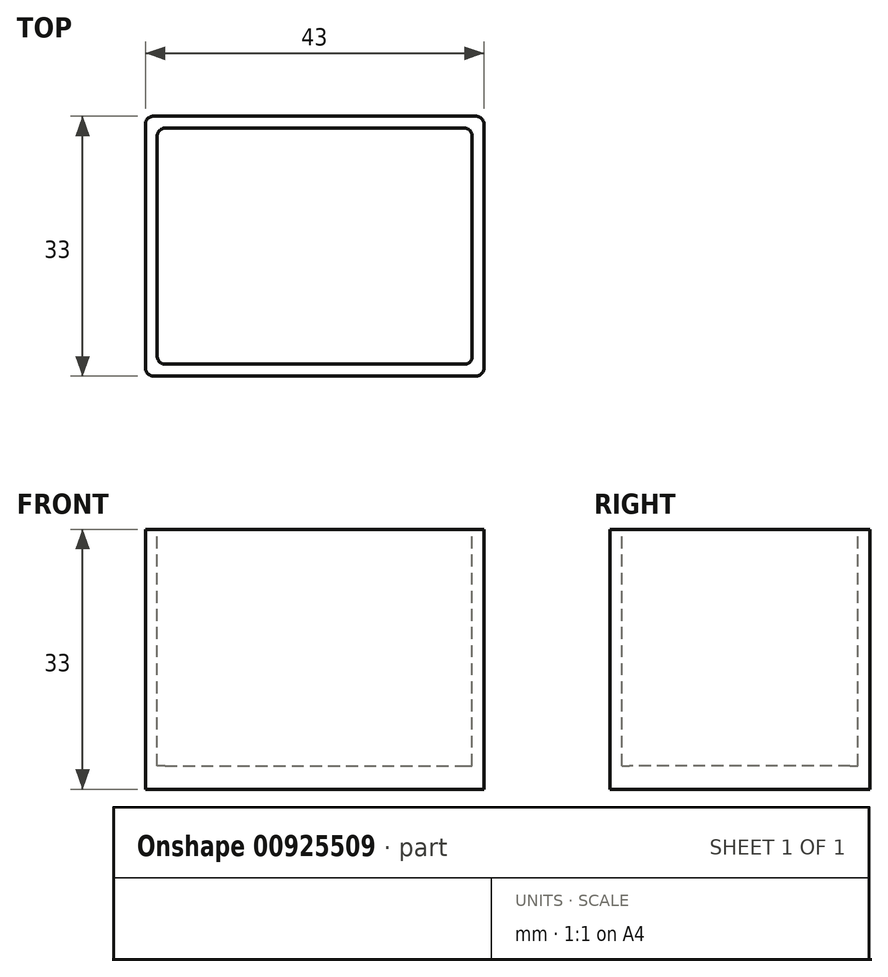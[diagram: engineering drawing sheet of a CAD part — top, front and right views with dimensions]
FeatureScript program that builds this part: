
annotation { "Feature Type Name" : "Feature", "Feature Type Description" : "" }
export const myFeature = defineFeature(function(context is Context, id is Id, definition is map)
    precondition{}
    {
        {
            var Q0;
            Q0=qCreatedBy(makeId("Top.planeOp"),FACE);
            var sketch = newSketch(context, id + "F0", { "sketchPlane" : qUnion([Q0])});
            skLineSegment(sketch, "E0.bottom", {"start": v(-21.5, 16.5) * mm, "end": v(21.5, 16.5) * mm});
            skLineSegment(sketch, "E0.top", {"start": v(-21.5, -16.5) * mm, "end": v(21.5, -16.5) * mm});
            skLineSegment(sketch, "E0.left", {"start": v(-21.5, 16.5) * mm, "end": v(-21.5, -16.5) * mm});
            skLineSegment(sketch, "E0.right", {"start": v(21.5, 16.5) * mm, "end": v(21.5, -16.5) * mm});
            skPoint(sketch, "E0.middle", {"position": v(0, 0) * mm});
            skSolve(sketch);
        }
        {
            var Q0;
            Q0=makeQuery(id+"F0.imprint","IMPRINT",FACE,{"disambiguationData":[TD([[makeQuery(id+"F0.imprint","IMPRINT",EDGE,{"derivedFrom":sQuery(id+"F0.wireOp",EDGE,"E0.bottom")}),-1.0]])]});
            extrude(context, id + "F1", {"entities" : qUnion([Q0]), "depth" : 33 * mm, "offsetDistance" : 25 * mm});
        }
        {
            var Q0;
            Q0=makeQuery(id+"F1.opExtrude","CAP_FACE",FACE,{"disambiguationData":[OSD([sQuery(id+"F0.wireOp",EDGE,"E0.bottom"),sQuery(id+"F0.wireOp",EDGE,"E0.top"),sQuery(id+"F0.wireOp",EDGE,"E0.left"),sQuery(id+"F0.wireOp",EDGE,"E0.right")])],"isStart":false});
            var sketch = newSketch(context, id + "F2", { "sketchPlane" : qUnion([Q0])});
            skLineSegment(sketch, "E1.bottom", {"start": v(-20, 15) * mm, "end": v(20, 15) * mm});
            skLineSegment(sketch, "E1.top", {"start": v(-20, -15) * mm, "end": v(20, -15) * mm});
            skLineSegment(sketch, "E1.left", {"start": v(-20, 15) * mm, "end": v(-20, -15) * mm});
            skLineSegment(sketch, "E1.right", {"start": v(20, 15) * mm, "end": v(20, -15) * mm});
            skPoint(sketch, "E1.middle", {"position": v(0, 0) * mm});
            skSolve(sketch);
        }
        {
            var Q0;
            Q0=makeQuery(id+"F2.imprint","IMPRINT",FACE,{"disambiguationData":[TD([[makeQuery(id+"F2.imprint","IMPRINT",EDGE,{"derivedFrom":sQuery(id+"F2.wireOp",EDGE,"E1.bottom")}),-1.0]])]});
            extrude(context, id + "F3", {"entities" : qUnion([Q0]), "operationType" : NewBodyOperationType.REMOVE, "oppositeDirection" : true, "depth" : 30 * mm, "offsetDistance" : 25 * mm});
        }
        {
            var Q0;
            Q0=makeQuery(id+"F1.opExtrude","SWEPT_EDGE",EDGE,{"disambiguationData":[OSD([sQuery(id+"F0.wireOp",EDGE,"E0.top"),sQuery(id+"F0.wireOp",EDGE,"E0.left")])]});
            var Q1;
            Q1=makeQuery(id+"F1.opExtrude","SWEPT_EDGE",EDGE,{"disambiguationData":[OSD([sQuery(id+"F0.wireOp",EDGE,"E0.top"),sQuery(id+"F0.wireOp",EDGE,"E0.right")])]});
            var Q2;
            Q2=makeQuery(id+"F1.opExtrude","SWEPT_EDGE",EDGE,{"disambiguationData":[OSD([sQuery(id+"F0.wireOp",EDGE,"E0.bottom"),sQuery(id+"F0.wireOp",EDGE,"E0.right")])]});
            var Q3;
            Q3=makeQuery(id+"F1.opExtrude","SWEPT_EDGE",EDGE,{"disambiguationData":[OSD([sQuery(id+"F0.wireOp",EDGE,"E0.bottom"),sQuery(id+"F0.wireOp",EDGE,"E0.left")])]});
            fillet(context, id + "F4", {"entities" : qUnion([Q0, Q1, Q2, Q3]), "radius" : 1 * mm, "tangentPropagation" : true, "allowEdgeOverflow" : false});
        }
        {
            var Q0;
            Q0=makeQuery(id+"F3.boolean.opBoolean","COPY",EDGE,{"derivedFrom":makeQuery(id+"F3.opExtrude","SWEPT_EDGE",EDGE,{"disambiguationData":[OSD([sQuery(id+"F2.wireOp",EDGE,"E1.top"),sQuery(id+"F2.wireOp",EDGE,"E1.left")])]})});
            var Q1;
            Q1=makeQuery(id+"F3.boolean.opBoolean","COPY",EDGE,{"derivedFrom":makeQuery(id+"F3.opExtrude","SWEPT_EDGE",EDGE,{"disambiguationData":[OSD([sQuery(id+"F2.wireOp",EDGE,"E1.bottom"),sQuery(id+"F2.wireOp",EDGE,"E1.left")])]})});
            var Q2;
            Q2=makeQuery(id+"F3.boolean.opBoolean","COPY",EDGE,{"derivedFrom":makeQuery(id+"F3.opExtrude","SWEPT_EDGE",EDGE,{"disambiguationData":[OSD([sQuery(id+"F2.wireOp",EDGE,"E1.bottom"),sQuery(id+"F2.wireOp",EDGE,"E1.right")])]})});
            var Q3;
            Q3=makeQuery(id+"F3.boolean.opBoolean","COPY",EDGE,{"derivedFrom":makeQuery(id+"F3.opExtrude","SWEPT_EDGE",EDGE,{"disambiguationData":[OSD([sQuery(id+"F2.wireOp",EDGE,"E1.top"),sQuery(id+"F2.wireOp",EDGE,"E1.right")])]})});
            fillet(context, id + "F5", {"entities" : qUnion([Q0, Q1, Q2, Q3]), "radius" : 1 * mm, "tangentPropagation" : true, "allowEdgeOverflow" : false});
        }
    });
